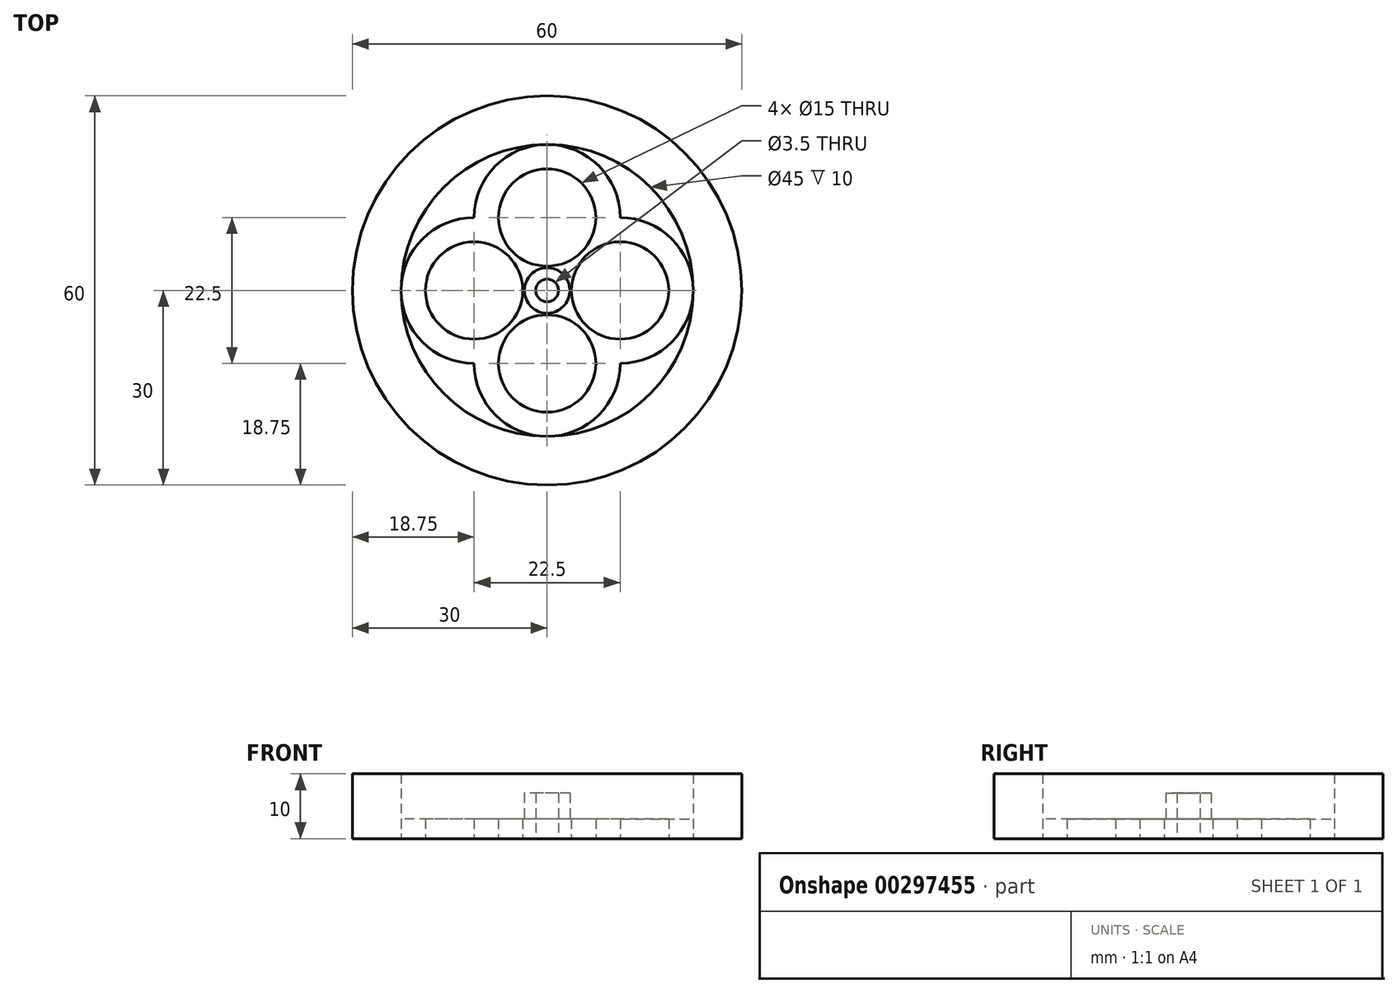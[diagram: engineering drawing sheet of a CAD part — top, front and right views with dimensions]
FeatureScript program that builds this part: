
annotation { "Feature Type Name" : "Feature", "Feature Type Description" : "" }
export const myFeature = defineFeature(function(context is Context, id is Id, definition is map)
    precondition{}
    {
        {
            var Q0;
            Q0=qCreatedBy(makeId("Top.planeOp"),FACE);
            var sketch = newSketch(context, id + "F0", { "sketchPlane" : qUnion([Q0])});
            skPoint(sketch, "E0", {"position": v(0, 0) * mm});
            skCircle(sketch, "E1", {"center": v(0, 0) * mm, "radius": 30 * mm});
            skCircle(sketch, "E2", {"center": v(0, 0) * mm, "radius": 22.5 * mm});
            skPoint(sketch, "E3", {"position": v(11.25, 0) * mm});
            skPoint(sketch, "E4", {"position": v(0, 11.25) * mm});
            skPoint(sketch, "E5", {"position": v(-11.25, 0) * mm});
            skPoint(sketch, "E6", {"position": v(0, -11.25) * mm});
            skCircle(sketch, "E7", {"center": v(0, 11.25) * mm, "radius": 11.25 * mm});
            skCircle(sketch, "E8", {"center": v(11.25, 0) * mm, "radius": 11.25 * mm});
            skCircle(sketch, "E9", {"center": v(-11.25, 0) * mm, "radius": 11.25 * mm});
            skCircle(sketch, "E10", {"center": v(0, -11.25) * mm, "radius": 11.25 * mm});
            skCircle(sketch, "E11", {"center": v(-11.25, 0) * mm, "radius": 7.5 * mm});
            skCircle(sketch, "E12", {"center": v(0, -11.25) * mm, "radius": 7.5 * mm});
            skCircle(sketch, "E13", {"center": v(11.25, 0) * mm, "radius": 7.5 * mm});
            skCircle(sketch, "E14", {"center": v(0, 11.25) * mm, "radius": 7.5 * mm});
            skCircle(sketch, "E15", {"center": v(0, 0) * mm, "radius": 1.75 * mm});
            skCircle(sketch, "E16", {"center": v(0, 0) * mm, "radius": 3.5 * mm});
            skSolve(sketch);
        }
        {
            var Q0;
            Q0=makeQuery(id+"F0.imprint","IMPRINT",FACE,{"disambiguationData":[TD([[makeQuery(id+"F0.imprint","IMPRINT",EDGE,{"derivedFrom":sQuery(id+"F0.wireOp",EDGE,"E1")}),1.0]])]});
            extrude(context, id + "F1", {"entities" : qUnion([Q0]), "depth" : 10 * mm});
        }
        {
            var Q0;
            {var subQ1=sQuery(id+"F0.wireOp",EDGE,"E9");var subQ6=sQuery(id+"F0.wireOp",EDGE,"E7");var subQ7=makeQuery(id+"F0.imprint","INTERSECT",VERTEX,{"derivedFrom":[subQ6,subQ1]});Q0=makeQuery(id+"F0.imprint","IMPRINT",FACE,{"disambiguationData":[TD([[makeQuery(id+"F0.imprint","IMPRINT",EDGE,{"disambiguationData":[TD([[subQ7,-1.0]])],"derivedFrom":subQ6}),-1.0]])]});}
            var Q1;
            {var subQ0=sQuery(id+"F0.wireOp",EDGE,"E9");var subQ1=sQuery(id+"F0.wireOp",EDGE,"E7");var subQ2=makeQuery(id+"F0.imprint","INTERSECT",VERTEX,{"derivedFrom":[subQ1,subQ0]});Q1=makeQuery(id+"F0.imprint","IMPRINT",FACE,{"disambiguationData":[TD([[makeQuery(id+"F0.imprint","IMPRINT",EDGE,{"disambiguationData":[TD([[subQ2,-1.0]])],"derivedFrom":subQ1}),1.0]])]});}
            var Q2;
            {var subQ0=sQuery(id+"F0.wireOp",EDGE,"E10");var subQ1=sQuery(id+"F0.wireOp",EDGE,"E9");var subQ2=makeQuery(id+"F0.imprint","INTERSECT",VERTEX,{"derivedFrom":[subQ1,subQ0]});Q2=makeQuery(id+"F0.imprint","IMPRINT",FACE,{"disambiguationData":[TD([[makeQuery(id+"F0.imprint","IMPRINT",EDGE,{"disambiguationData":[TD([[subQ2,-1.0]])],"derivedFrom":subQ1}),1.0]])]});}
            var Q3;
            {var subQ3=sQuery(id+"F0.wireOp",EDGE,"E16");var subQ5=sQuery(id+"F0.wireOp",EDGE,"E8");var subQ10=makeQuery(id+"F0.imprint","INTERSECT",VERTEX,{"disambiguationData":[OD(1.0)],"derivedFrom":[subQ5,subQ3]});Q3=makeQuery(id+"F0.imprint","IMPRINT",FACE,{"disambiguationData":[TD([[makeQuery(id+"F0.imprint","IMPRINT",EDGE,{"disambiguationData":[TD([[subQ10,-1.0]])],"derivedFrom":subQ5}),1.0]])]});}
            var Q4;
            {var subQ3=sQuery(id+"F0.wireOp",EDGE,"E16");var subQ5=sQuery(id+"F0.wireOp",EDGE,"E7");var subQ10=makeQuery(id+"F0.imprint","INTERSECT",VERTEX,{"disambiguationData":[OD(1.0)],"derivedFrom":[subQ5,subQ3]});Q4=makeQuery(id+"F0.imprint","IMPRINT",FACE,{"disambiguationData":[TD([[makeQuery(id+"F0.imprint","IMPRINT",EDGE,{"disambiguationData":[TD([[subQ10,-1.0]])],"derivedFrom":subQ5}),1.0]])]});}
            var Q5;
            {var subQ1=sQuery(id+"F0.wireOp",EDGE,"E7");var subQ8=makeQuery(id+"F0.imprint","INTERSECT",VERTEX,{"derivedFrom":[sQuery(id+"F0.wireOp",EDGE,"E2"),subQ1]});Q5=makeQuery(id+"F0.imprint","IMPRINT",FACE,{"disambiguationData":[TD([[makeQuery(id+"F0.imprint","IMPRINT",EDGE,{"disambiguationData":[TD([[subQ8,1.0]])],"derivedFrom":subQ1}),1.0]])]});}
            var Q6;
            {var subQ0=sQuery(id+"F0.wireOp",EDGE,"E8");var subQ4=sQuery(id+"F0.wireOp",EDGE,"E7");var subQ5=makeQuery(id+"F0.imprint","INTERSECT",VERTEX,{"derivedFrom":[subQ4,subQ0]});Q6=makeQuery(id+"F0.imprint","IMPRINT",FACE,{"disambiguationData":[TD([[makeQuery(id+"F0.imprint","IMPRINT",EDGE,{"disambiguationData":[TD([[subQ5,1.0]])],"derivedFrom":subQ4}),-1.0]])]});}
            var Q7;
            {var subQ4=sQuery(id+"F0.wireOp",EDGE,"E12");var subQ6=sQuery(id+"F0.wireOp",EDGE,"E8");var subQ8=makeQuery(id+"F0.imprint","INTERSECT",VERTEX,{"disambiguationData":[OD(1.0)],"derivedFrom":[subQ6,subQ4]});Q7=makeQuery(id+"F0.imprint","IMPRINT",FACE,{"disambiguationData":[TD([[makeQuery(id+"F0.imprint","IMPRINT",EDGE,{"disambiguationData":[TD([[subQ8,-1.0]])],"derivedFrom":subQ6}),-1.0]])]});}
            var Q8;
            {var subQ0=sQuery(id+"F0.wireOp",EDGE,"E16");var subQ1=sQuery(id+"F0.wireOp",EDGE,"E8");var subQ2=makeQuery(id+"F0.imprint","INTERSECT",VERTEX,{"disambiguationData":[OD(1.0)],"derivedFrom":[subQ1,subQ0]});Q8=makeQuery(id+"F0.imprint","IMPRINT",FACE,{"disambiguationData":[TD([[makeQuery(id+"F0.imprint","IMPRINT",EDGE,{"disambiguationData":[TD([[subQ2,-1.0]])],"derivedFrom":subQ1}),-1.0]])]});}
            var Q9;
            {var subQ0=sQuery(id+"F0.wireOp",EDGE,"E11");var subQ1=sQuery(id+"F0.wireOp",EDGE,"E7");var subQ2=makeQuery(id+"F0.imprint","INTERSECT",VERTEX,{"disambiguationData":[OD(1.0)],"derivedFrom":[subQ1,subQ0]});Q9=makeQuery(id+"F0.imprint","IMPRINT",FACE,{"disambiguationData":[TD([[makeQuery(id+"F0.imprint","IMPRINT",EDGE,{"disambiguationData":[TD([[subQ2,-1.0]])],"derivedFrom":subQ1}),-1.0]])]});}
            var Q10;
            {var subQ0=sQuery(id+"F0.wireOp",EDGE,"E16");var subQ1=sQuery(id+"F0.wireOp",EDGE,"E7");var subQ2=makeQuery(id+"F0.imprint","INTERSECT",VERTEX,{"disambiguationData":[OD(1.0)],"derivedFrom":[subQ1,subQ0]});Q10=makeQuery(id+"F0.imprint","IMPRINT",FACE,{"disambiguationData":[TD([[makeQuery(id+"F0.imprint","IMPRINT",EDGE,{"disambiguationData":[TD([[subQ2,-1.0]])],"derivedFrom":subQ1}),-1.0]])]});}
            var Q11;
            {var subQ0=sQuery(id+"F0.wireOp",EDGE,"E14");var subQ1=sQuery(id+"F0.wireOp",EDGE,"E8");var subQ2=makeQuery(id+"F0.imprint","INTERSECT",VERTEX,{"disambiguationData":[OD(1.0)],"derivedFrom":[subQ1,subQ0]});Q11=makeQuery(id+"F0.imprint","IMPRINT",FACE,{"disambiguationData":[TD([[makeQuery(id+"F0.imprint","IMPRINT",EDGE,{"disambiguationData":[TD([[subQ2,-1.0]])],"derivedFrom":subQ1}),-1.0]])]});}
            extrude(context, id + "F2", {"entities" : qUnion([Q0, Q1, Q2, Q3, Q4, Q5, Q6, Q7, Q8, Q9, Q10, Q11]), "operationType" : NewBodyOperationType.ADD, "depth" : 3 * mm});
        }
        {
            var Q0;
            {var subQ0=sQuery(id+"F0.wireOp",EDGE,"E15");var subQ1=sQuery(id+"F0.wireOp",EDGE,"E7");var subQ2=makeQuery(id+"F0.imprint","INTERSECT",VERTEX,{"disambiguationData":[OD(1.0)],"derivedFrom":[subQ1,subQ0]});Q0=makeQuery(id+"F0.imprint","IMPRINT",FACE,{"disambiguationData":[TD([[makeQuery(id+"F0.imprint","IMPRINT",EDGE,{"disambiguationData":[TD([[subQ2,-1.0]])],"derivedFrom":subQ1}),1.0]])]});}
            var Q1;
            {var subQ0=sQuery(id+"F0.wireOp",EDGE,"E16");var subQ1=sQuery(id+"F0.wireOp",EDGE,"E7");var subQ2=makeQuery(id+"F0.imprint","INTERSECT",VERTEX,{"disambiguationData":[OD(0.0)],"derivedFrom":[subQ1,subQ0]});Q1=makeQuery(id+"F0.imprint","IMPRINT",FACE,{"disambiguationData":[TD([[makeQuery(id+"F0.imprint","IMPRINT",EDGE,{"disambiguationData":[TD([[subQ2,-1.0]])],"derivedFrom":subQ1}),1.0]])]});}
            var Q2;
            {var subQ0=sQuery(id+"F0.wireOp",EDGE,"E16");var subQ1=sQuery(id+"F0.wireOp",EDGE,"E9");var subQ2=makeQuery(id+"F0.imprint","INTERSECT",VERTEX,{"disambiguationData":[OD(1.0)],"derivedFrom":[subQ1,subQ0]});Q2=makeQuery(id+"F0.imprint","IMPRINT",FACE,{"disambiguationData":[TD([[makeQuery(id+"F0.imprint","IMPRINT",EDGE,{"disambiguationData":[TD([[subQ2,-1.0]])],"derivedFrom":subQ1}),1.0]])]});}
            var Q3;
            {var subQ0=sQuery(id+"F0.wireOp",EDGE,"E15");var subQ1=sQuery(id+"F0.wireOp",EDGE,"E8");var subQ2=makeQuery(id+"F0.imprint","INTERSECT",VERTEX,{"disambiguationData":[OD(1.0)],"derivedFrom":[subQ1,subQ0]});Q3=makeQuery(id+"F0.imprint","IMPRINT",FACE,{"disambiguationData":[TD([[makeQuery(id+"F0.imprint","IMPRINT",EDGE,{"disambiguationData":[TD([[subQ2,-1.0]])],"derivedFrom":subQ1}),1.0]])]});}
            var Q4;
            {var subQ0=sQuery(id+"F0.wireOp",EDGE,"E15");var subQ1=sQuery(id+"F0.wireOp",EDGE,"E8");var subQ2=makeQuery(id+"F0.imprint","INTERSECT",VERTEX,{"disambiguationData":[OD(1.0)],"derivedFrom":[subQ1,subQ0]});Q4=makeQuery(id+"F0.imprint","IMPRINT",FACE,{"disambiguationData":[TD([[makeQuery(id+"F0.imprint","IMPRINT",EDGE,{"disambiguationData":[TD([[subQ2,-1.0]])],"derivedFrom":subQ1}),-1.0]])]});}
            var Q5;
            {var subQ0=sQuery(id+"F0.wireOp",EDGE,"E16");var subQ1=sQuery(id+"F0.wireOp",EDGE,"E7");var subQ2=makeQuery(id+"F0.imprint","INTERSECT",VERTEX,{"disambiguationData":[OD(0.0)],"derivedFrom":[subQ1,subQ0]});Q5=makeQuery(id+"F0.imprint","IMPRINT",FACE,{"disambiguationData":[TD([[makeQuery(id+"F0.imprint","IMPRINT",EDGE,{"disambiguationData":[TD([[subQ2,-1.0]])],"derivedFrom":subQ1}),-1.0]])]});}
            var Q6;
            {var subQ0=sQuery(id+"F0.wireOp",EDGE,"E15");var subQ1=sQuery(id+"F0.wireOp",EDGE,"E7");var subQ2=makeQuery(id+"F0.imprint","INTERSECT",VERTEX,{"disambiguationData":[OD(1.0)],"derivedFrom":[subQ1,subQ0]});Q6=makeQuery(id+"F0.imprint","IMPRINT",FACE,{"disambiguationData":[TD([[makeQuery(id+"F0.imprint","IMPRINT",EDGE,{"disambiguationData":[TD([[subQ2,-1.0]])],"derivedFrom":subQ1}),-1.0]])]});}
            var Q7;
            {var subQ0=sQuery(id+"F0.wireOp",EDGE,"E16");var subQ1=sQuery(id+"F0.wireOp",EDGE,"E8");var subQ2=makeQuery(id+"F0.imprint","INTERSECT",VERTEX,{"disambiguationData":[OD(0.0)],"derivedFrom":[subQ1,subQ0]});Q7=makeQuery(id+"F0.imprint","IMPRINT",FACE,{"disambiguationData":[TD([[makeQuery(id+"F0.imprint","IMPRINT",EDGE,{"disambiguationData":[TD([[subQ2,-1.0]])],"derivedFrom":subQ1}),-1.0]])]});}
            extrude(context, id + "F3", {"entities" : qUnion([Q0, Q1, Q2, Q3, Q4, Q5, Q6, Q7]), "operationType" : NewBodyOperationType.ADD, "depth" : 7 * mm});
        }
        {
            var Q0;
            Q0=makeQuery(id+"F1.opExtrude","SWEPT_BODY",BODY,{"disambiguationData":[OSD([sQuery(id+"F0.wireOp",EDGE,"E1"),sQuery(id+"F0.wireOp",EDGE,"E2")])]});
            var Q1;
            Q1=makeQuery(id+"F2.opExtrude","SWEPT_BODY",BODY,{"disambiguationData":[OSD([sQuery(id+"F0.wireOp",EDGE,"E7"),sQuery(id+"F0.wireOp",EDGE,"E8"),sQuery(id+"F0.wireOp",EDGE,"E9"),sQuery(id+"F0.wireOp",EDGE,"E10"),sQuery(id+"F0.wireOp",EDGE,"E11"),sQuery(id+"F0.wireOp",EDGE,"E12"),sQuery(id+"F0.wireOp",EDGE,"E13"),sQuery(id+"F0.wireOp",EDGE,"E14"),sQuery(id+"F0.wireOp",EDGE,"E16")])]});
            booleanBodies(context, id + "F4", {"operationType" : BooleanOperationType.INTERSECTION, "tools" : qUnion([Q0, Q1]), "keepTools" : true});
        }
    });
